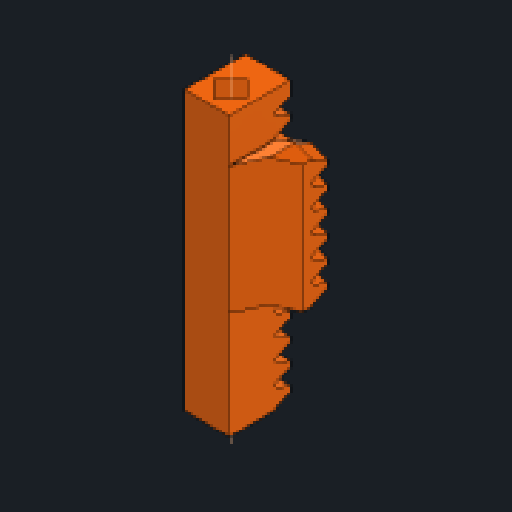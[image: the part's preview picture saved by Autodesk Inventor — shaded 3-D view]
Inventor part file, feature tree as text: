
AUTODESK INVENTOR PART (.ipt)
format: ipt  version: 2023.2 (Build 272271030, 271C)  size: 650,240 bytes
history: native  units: mm
features: sketch x5, projected_geometry x4, extrude x3, sweep x1, pattern_linear x1, other x1, chamfer x1
ambient origin geometry x8: Origin, YZ Plane, XZ Plane, XY Plane, X Axis, Y Axis, Z Axis, Center Point
bodies: Solid1 (feature_tree)
feature tree (16):
  extrude  "Extrusion1"  Depth=34.557519mm
  sweep  "Sweep1"
  pattern_linear  "Rectangular Pattern1"  Spacing1=0.38mm  [1 undecoded]
  sketch  "Sketch4"  dims[d6=1.570796mm]
  extrude  "Extrusion8"  Depth=6.6mm
  other  "Work Axis1"
  chamfer  "Chamfer2"  Distance=5.0mm
  extrude  "Extrusion11"  Depth=6.6mm
  sketch  "Sketch1"  dims[d0=12.0mm d1=34.557519mm]
  sketch  "Sketch2"  dims[d2=9.0mm d3=0.0mm d4=1.0mm]
  projected_geometry  "Projected Loop1"
  sketch  "Sketch3"  dims[d5=1.25mm]
  projected_geometry  "Projected Loop2"
  sketch  "Sketch11"  dims[d7=12.217305mm d17=0.38mm d27=7.0mm d28=5.0mm d29=3.490659mm d30=0.0mm d31=0.0mm d32=120.0mm d34=3.141593mm d56=0.0mm d57=0.0mm d60=3.5mm d61=3.3mm d62=5.5mm d64=5.4mm d65=2.0mm d66=45.0deg d71=6.6mm d72=0.0mm d73=0.0mm d43=0.5mm d44=0.872665mm d45=0.5mm d46=0.872665mm]
  projected_geometry  "Projected Loop24"
  projected_geometry  "Projected Loop25"
note: 1 required parameter value undecoded (feature->parameter linkage not recoverable at this tier; creation-order binding heuristic only, values carry confidence <= 0.55)
